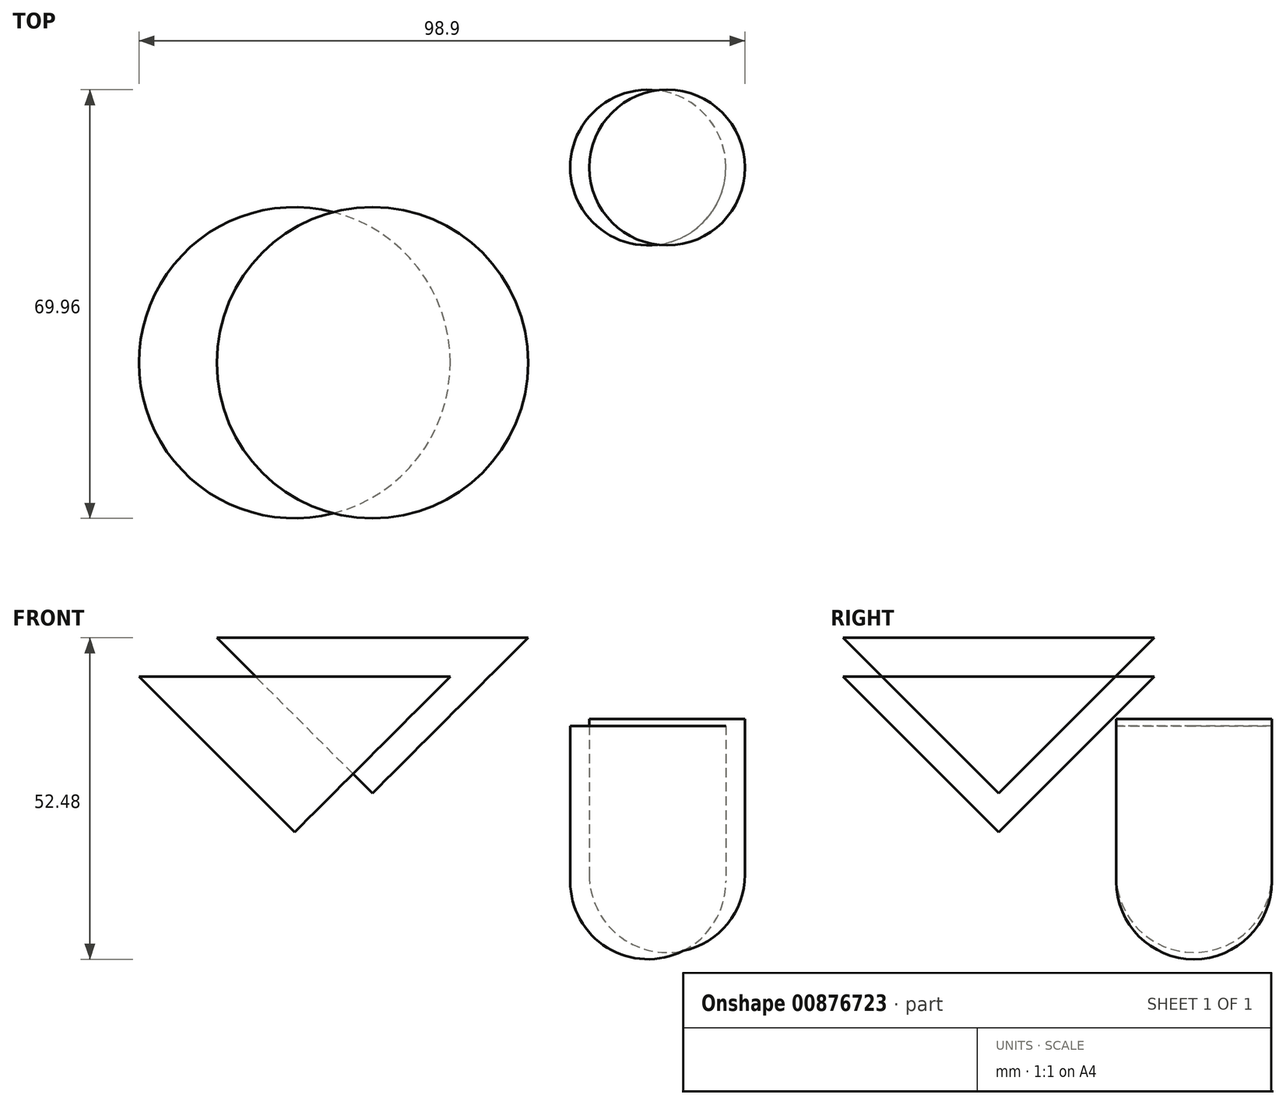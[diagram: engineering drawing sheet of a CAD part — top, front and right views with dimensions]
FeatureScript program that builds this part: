
annotation { "Feature Type Name" : "Feature", "Feature Type Description" : "" }
export const myFeature = defineFeature(function(context is Context, id is Id, definition is map)
    precondition{}
    {
        {
            var Q0;
            Q0=qCreatedBy(makeId("Top.planeOp"),FACE);
            var sketch = newSketch(context, id + "F0", { "sketchPlane" : qUnion([Q0])});
            skCircle(sketch, "E0", {"center": v(0, 0) * mm, "radius": 13.57 * mm});
            skCircle(sketch, "E1", {"center": v(-9.73, 0) * mm, "radius": 13.3 * mm});
            skCircle(sketch, "E2", {"center": v(6.18, 0) * mm, "radius": 12.52 * mm});
            skCircle(sketch, "E3", {"center": v(37.73, 31.86) * mm, "radius": 12.7 * mm});
            skLineSegment(sketch, "E4", {"start": v(25.03, 31.86) * mm, "end": v(50.43, 31.86) * mm});
            skSolve(sketch);
        }
        {
            var Q0;
            {var subQ0=sQuery(id+"F0.wireOp",EDGE,"E4");Q0=makeQuery(id+"F0.imprint","IMPRINT",FACE,{"disambiguationData":[TD([[makeQuery(id+"F0.imprint","IMPRINT",EDGE,{"derivedFrom":subQ0}),1.0]])]});}
            var Q1;
            Q1=sQuery(id+"F0.wireOp",EDGE,"E4");
            revolve(context, id + "F1", {"surfaceOperationType" : NewSurfaceOperationType.NEW, "entities" : qUnion([Q0]), "axis" : qUnion([Q1]), "revolveType" : RevolveType.ONE_DIRECTION, "oppositeDirection" : true, "angle" : 180 * degree});
        }
        {
            var Q0;
            Q0=makeQuery(id+"F1.opRevolve","CAP_FACE",FACE,{"disambiguationData":[OSD([sQuery(id+"F0.wireOp",EDGE,"E3"),sQuery(id+"F0.wireOp",EDGE,"E4")])],"isStart":true});
            extrude(context, id + "F2", {"entities" : qUnion([Q0]), "operationType" : NewBodyOperationType.ADD, "depth" : 25.4 * mm, "offsetDistance" : 25.4 * mm});
        }
        {
            var Q0;
            Q0=makeQuery(id+"F1.opRevolve","SWEPT_BODY",BODY,{"disambiguationData":[OSD([sQuery(id+"F0.wireOp",EDGE,"E3"),sQuery(id+"F0.wireOp",EDGE,"E4")])]});
            transform(context, id + "F3", {"entities" : qUnion([Q0]), "transformType" : TransformType.TRANSLATION_3D, "dx" : 3.12 * mm, "dy" : 0 * mm, "dz" : 1.1 * mm, "makeCopy" : true});
        }
        {
            var Q0;
            Q0=qCreatedBy(makeId("Front.planeOp"),FACE);
            var sketch = newSketch(context, id + "F4", { "sketchPlane" : qUnion([Q0])});
            skLineSegment(sketch, "E5", {"start": v(-45.35, 33.43) * mm, "end": v(-19.95, 33.43) * mm});
            skLineSegment(sketch, "E6", {"start": v(-19.95, 33.43) * mm, "end": v(-19.95, 8.03) * mm});
            skLineSegment(sketch, "E7", {"start": v(-19.95, 8.03) * mm, "end": v(-45.35, 33.43) * mm});
            skSolve(sketch);
        }
        {
            var Q0;
            Q0=makeQuery(id+"F4.imprint","IMPRINT",FACE,{"disambiguationData":[TD([[makeQuery(id+"F4.imprint","IMPRINT",EDGE,{"derivedFrom":sQuery(id+"F4.wireOp",EDGE,"E5")}),-1.0]])]});
            var Q1;
            Q1=sQuery(id+"F4.wireOp",EDGE,"E6");
            revolve(context, id + "F5", {"surfaceOperationType" : NewSurfaceOperationType.NEW, "entities" : qUnion([Q0]), "axis" : qUnion([Q1]), "revolveType" : RevolveType.FULL});
        }
        {
            var Q0;
            Q0=makeQuery(id+"F5.opRevolve","SWEPT_BODY",BODY,{"disambiguationData":[OSD([sQuery(id+"F4.wireOp",EDGE,"E5"),sQuery(id+"F4.wireOp",EDGE,"E6"),sQuery(id+"F4.wireOp",EDGE,"E7")])]});
            transform(context, id + "F6", {"entities" : qUnion([Q0]), "transformType" : TransformType.TRANSLATION_3D, "dx" : 12.7 * mm, "dy" : 0 * mm, "dz" : 6.35 * mm, "makeCopy" : true});
        }
    });
